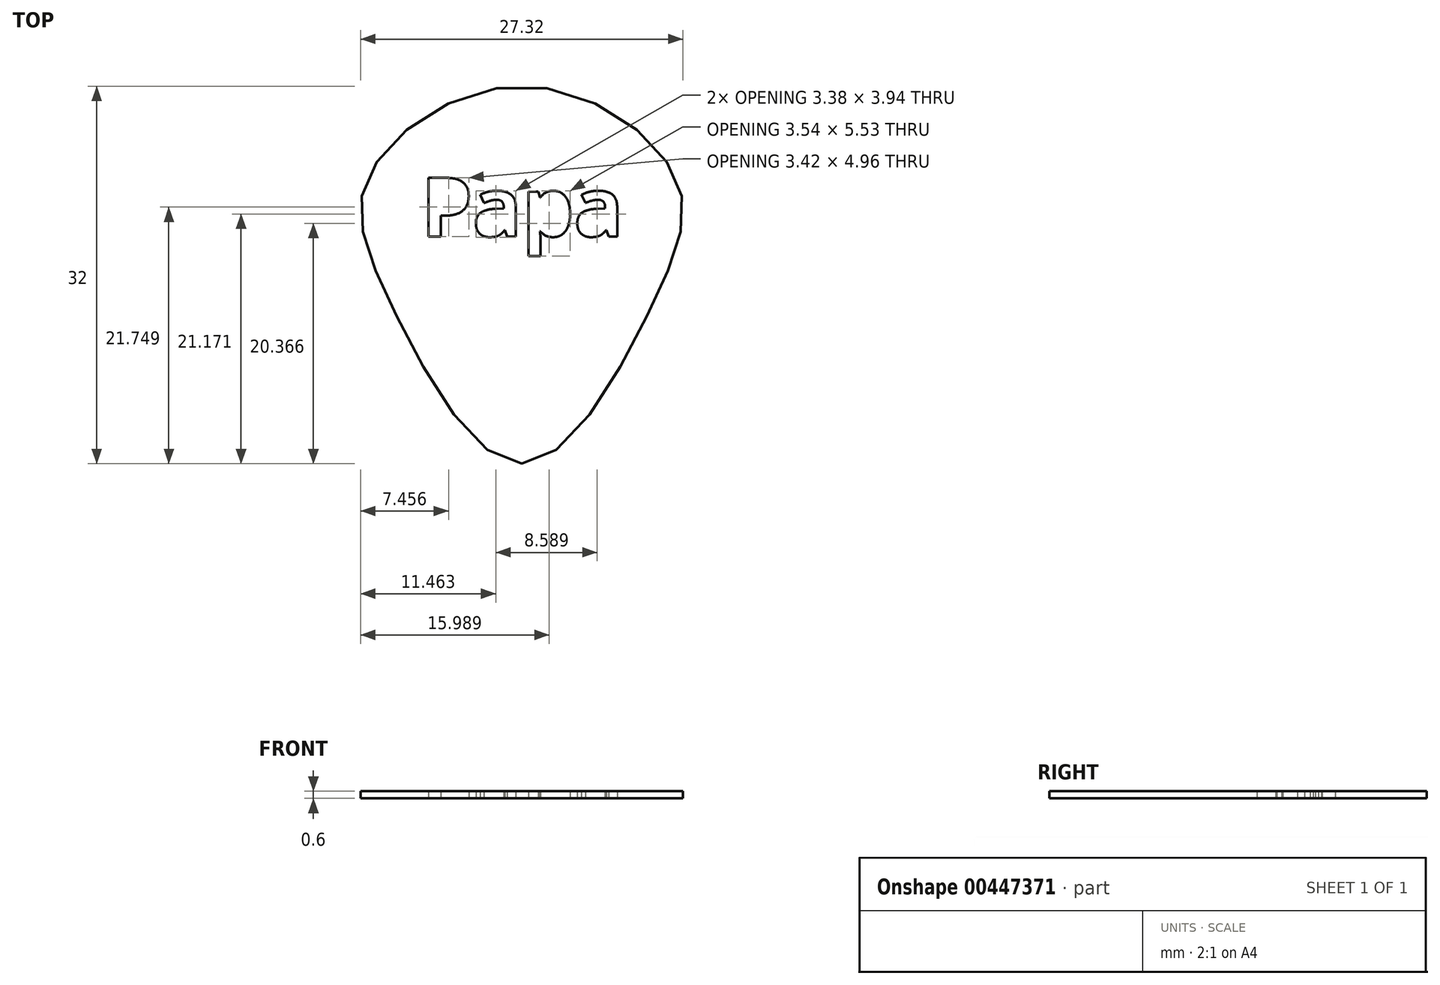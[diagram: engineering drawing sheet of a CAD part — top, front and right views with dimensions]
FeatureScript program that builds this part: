
annotation { "Feature Type Name" : "Feature", "Feature Type Description" : "" }
export const myFeature = defineFeature(function(context is Context, id is Id, definition is map)
    precondition{}
    {
        {
            var Q0;
            Q0=qCreatedBy(makeId("Top.planeOp"),FACE);
            var sketch = newSketch(context, id + "F0", { "sketchPlane" : qUnion([Q0])});
            skPoint(sketch, "E0", {"position": v(-13, 11) * mm});
            skPoint(sketch, "E1", {"position": v(13, 11) * mm});
            skPoint(sketch, "E2", {"position": v(0, -13.35) * mm});
            skPoint(sketch, "E3", {"position": v(0, 18.65) * mm});
            skPoint(sketch, "E4", {"position": v(-11, 0) * mm});
            skPoint(sketch, "E5", {"position": v(11, 0) * mm});
            skFitSpline(sketch, "E6", {"points": [v(0, -13.35) * mm, v(-11, 0) * mm, v(-13, 11) * mm, v(0, 18.65) * mm, v(13, 11) * mm, v(11, 0) * mm, v(0, -13.35) * mm]});
            skText(sketch, "E7", { "text": "Papa", "fontName": "OpenSans-Bold.ttf"});
            const initialGuessF0  = {"E7": [-0.00854, 0.00592, 1, 0, 0.005]};
            skSetInitialGuess(sketch, initialGuessF0);
            skSolve(sketch);
        }
        {
            var Q0;
            Q0=makeQuery(id+"F0.imprint","IMPRINT",FACE,{"disambiguationData":[TD([[makeQuery(id+"F0.imprint","IMPRINT",EDGE,{"derivedFrom":sQuery(id+"F0.wireOp",EDGE,"E6")}),-1.0]])]});
            extrude(context, id + "F1", {"entities" : qUnion([Q0]), "depth" : 0.6 * mm});
        }
    });
